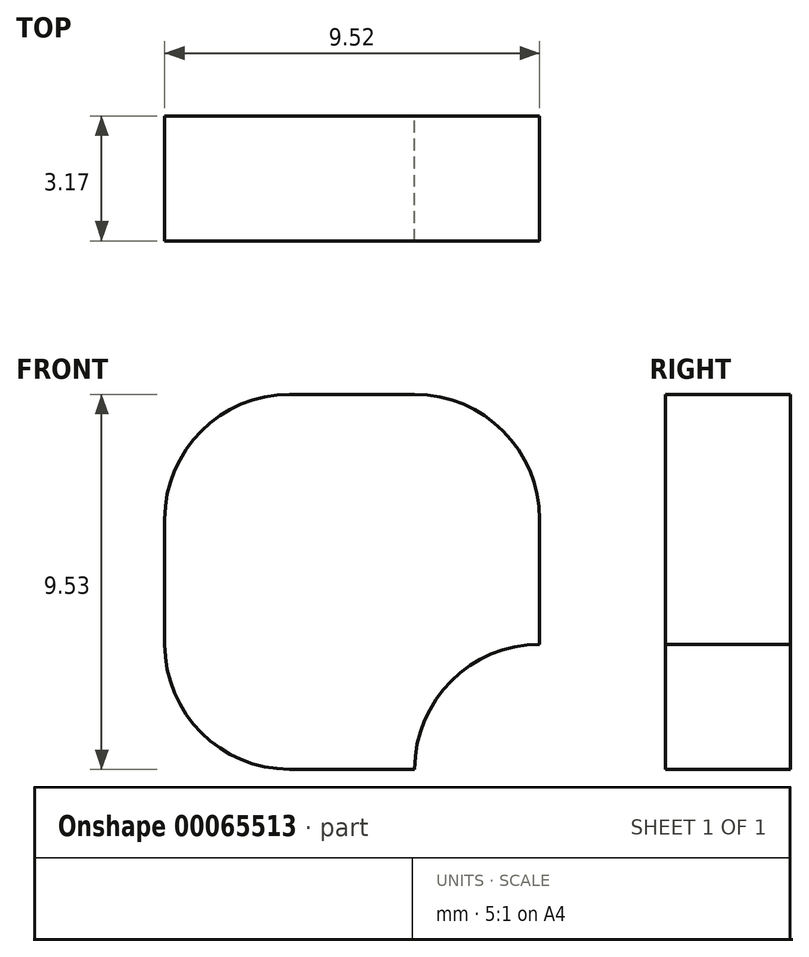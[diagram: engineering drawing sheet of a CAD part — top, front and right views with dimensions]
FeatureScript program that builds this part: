
annotation { "Feature Type Name" : "Feature", "Feature Type Description" : "" }
export const myFeature = defineFeature(function(context is Context, id is Id, definition is map)
    precondition{}
    {
        {
            var Q0;
            Q0=qCreatedBy(makeId("Front.planeOp"),FACE);
            var sketch = newSketch(context, id + "F0", { "sketchPlane" : qUnion([Q0])});
            skLineSegment(sketch, "E0.bottom", {"start": v(31.83, -1.16) * mm, "end": v(88.98, -1.16) * mm});
            skLineSegment(sketch, "E0.top", {"start": v(31.83, -20.21) * mm, "end": v(88.98, -20.21) * mm});
            skLineSegment(sketch, "E0.left", {"start": v(31.83, -1.16) * mm, "end": v(31.83, -20.21) * mm});
            skLineSegment(sketch, "E0.right", {"start": v(88.98, -1.16) * mm, "end": v(88.98, -20.21) * mm});
            skLineSegment(sketch, "E1.bottom", {"start": v(31.83, -1.16) * mm, "end": v(41.35, -1.16) * mm});
            skLineSegment(sketch, "E1.top", {"start": v(31.83, -10.69) * mm, "end": v(41.35, -10.69) * mm});
            skLineSegment(sketch, "E1.left", {"start": v(31.83, -1.16) * mm, "end": v(31.83, -10.69) * mm});
            skLineSegment(sketch, "E1.right", {"start": v(41.35, -1.16) * mm, "end": v(41.35, -10.69) * mm});
            skLineSegment(sketch, "E2.bottom", {"start": v(88.98, -20.21) * mm, "end": v(79.45, -20.21) * mm});
            skLineSegment(sketch, "E2.top", {"start": v(88.98, -10.69) * mm, "end": v(79.45, -10.69) * mm});
            skLineSegment(sketch, "E2.left", {"start": v(88.98, -20.21) * mm, "end": v(88.98, -10.69) * mm});
            skLineSegment(sketch, "E2.right", {"start": v(79.45, -20.21) * mm, "end": v(79.45, -10.69) * mm});
            skCircle(sketch, "E3", {"center": v(41.35, -10.69) * mm, "radius": 3.18 * mm});
            skCircle(sketch, "E4", {"center": v(79.45, -10.69) * mm, "radius": 3.18 * mm});
            skSolve(sketch);
        }
        {
            var Q0;
            {var subQ4=sQuery(id+"F0.wireOp",EDGE,"E0.bottom");Q0=makeQuery(id+"F0.imprint","IMPRINT",FACE,{"disambiguationData":[TD([[makeQuery(id+"F0.imprint","IMPRINT",EDGE,{"derivedFrom":subQ4}),-1.0]])]});}
            var Q1;
            {var subQ1=sQuery(id+"F0.wireOp",EDGE,"E1.bottom");Q1=makeQuery(id+"F0.imprint","IMPRINT",FACE,{"disambiguationData":[TD([[makeQuery(id+"F0.imprint","IMPRINT",EDGE,{"derivedFrom":subQ1}),-1.0]])]});}
            var Q2;
            {var subQ1=sQuery(id+"F0.wireOp",EDGE,"E2.bottom");Q2=makeQuery(id+"F0.imprint","IMPRINT",FACE,{"disambiguationData":[TD([[makeQuery(id+"F0.imprint","IMPRINT",EDGE,{"derivedFrom":subQ1}),-1.0]])]});}
            extrude(context, id + "F1", {"entities" : qUnion([Q0, Q1, Q2]), "depth" : 3.17 * mm});
        }
        {
            var Q0;
            Q0=makeQuery(id+"F1.opExtrude","SWEPT_EDGE",EDGE,{"disambiguationData":[OSD([sQuery(id+"F0.wireOp",EDGE,"E1.bottom"),sQuery(id+"F0.wireOp",EDGE,"E1.left")])]});
            var Q1;
            Q1=makeQuery(id+"F1.opExtrude","SWEPT_EDGE",EDGE,{"disambiguationData":[OSD([sQuery(id+"F0.wireOp",EDGE,"E0.top"),sQuery(id+"F0.wireOp",EDGE,"E0.left")])]});
            var Q2;
            Q2=makeQuery(id+"F1.opExtrude","SWEPT_EDGE",EDGE,{"disambiguationData":[OSD([sQuery(id+"F0.wireOp",EDGE,"E2.bottom"),sQuery(id+"F0.wireOp",EDGE,"E2.left")])]});
            var Q3;
            Q3=makeQuery(id+"F1.opExtrude","SWEPT_EDGE",EDGE,{"disambiguationData":[OSD([sQuery(id+"F0.wireOp",EDGE,"E0.bottom"),sQuery(id+"F0.wireOp",EDGE,"E0.right")])]});
            fillet(context, id + "F2", {"entities" : qUnion([Q0, Q1, Q2, Q3]), "radius" : 3.17 * mm, "tangentPropagation" : true, "allowEdgeOverflow" : false});
        }
    });
